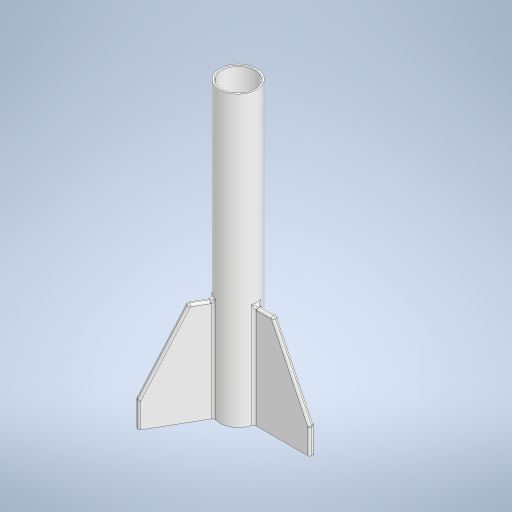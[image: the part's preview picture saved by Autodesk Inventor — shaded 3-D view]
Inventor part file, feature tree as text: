
AUTODESK INVENTOR PART (.ipt)
format: ipt  version: 2024 (Build 280153000, 153)  size: 494,592 bytes
history: native  units: mm
features: other x10, extrude x7, fillet x3, plane x3, pattern_circular x1
ambient origin geometry x8: Origin, YZ Plane, XZ Plane, XY Plane, X Axis, Y Axis, Z Axis, Center Point
bodies: body_sketch (feature_tree), body_extrude (feature_tree), body_top_fillet (feature_tree)
feature tree (24):
  other  "rocket_body"
  other  "fin_sketch"
  extrude  "fin_extrude"  Depth=19.4mm
  fillet  "fin_fillet"  Radius=21.8mm
  fillet  "fin_leading_edge_fillet"  Radius=170.0mm
  pattern_circular  "fin_pattern"  [2 undecoded]
  other  "fin_interior_cut_sketch"
  extrude  "fin_interior_cut"  Depth=60.0mm
  plane  "Work Plane6"
  other  "lug_sketch"
  extrude  "lug_extrude"  Depth=43.6mm
  other  "lug_hole_sketch"
  extrude  "lug_hole_cut"  Depth=21.8mm
  fillet  "lug_fillet"  Radius=15.0mm
  other  "bottom_hold_sketch"
  extrude  "bottom_hold_extrude"  Depth=3.2mm TaperAngle=0.0deg
  other  "top_hold_sketch"
  other  "top_hold_revolve"
  plane  "Work Plane10"
  other  "cord_attachment_sketch"
  extrude  "cord_attachment_extrude"  Depth=1.6mm
  other  "attachment_hole_sketch"
  extrude  "attachment_hole_cut"  Depth=1.2mm
  plane  "Work Plane5"
note: 2 required parameter values undecoded (feature->parameter linkage not recoverable at this tier; creation-order binding heuristic only, values carry confidence <= 0.55)
